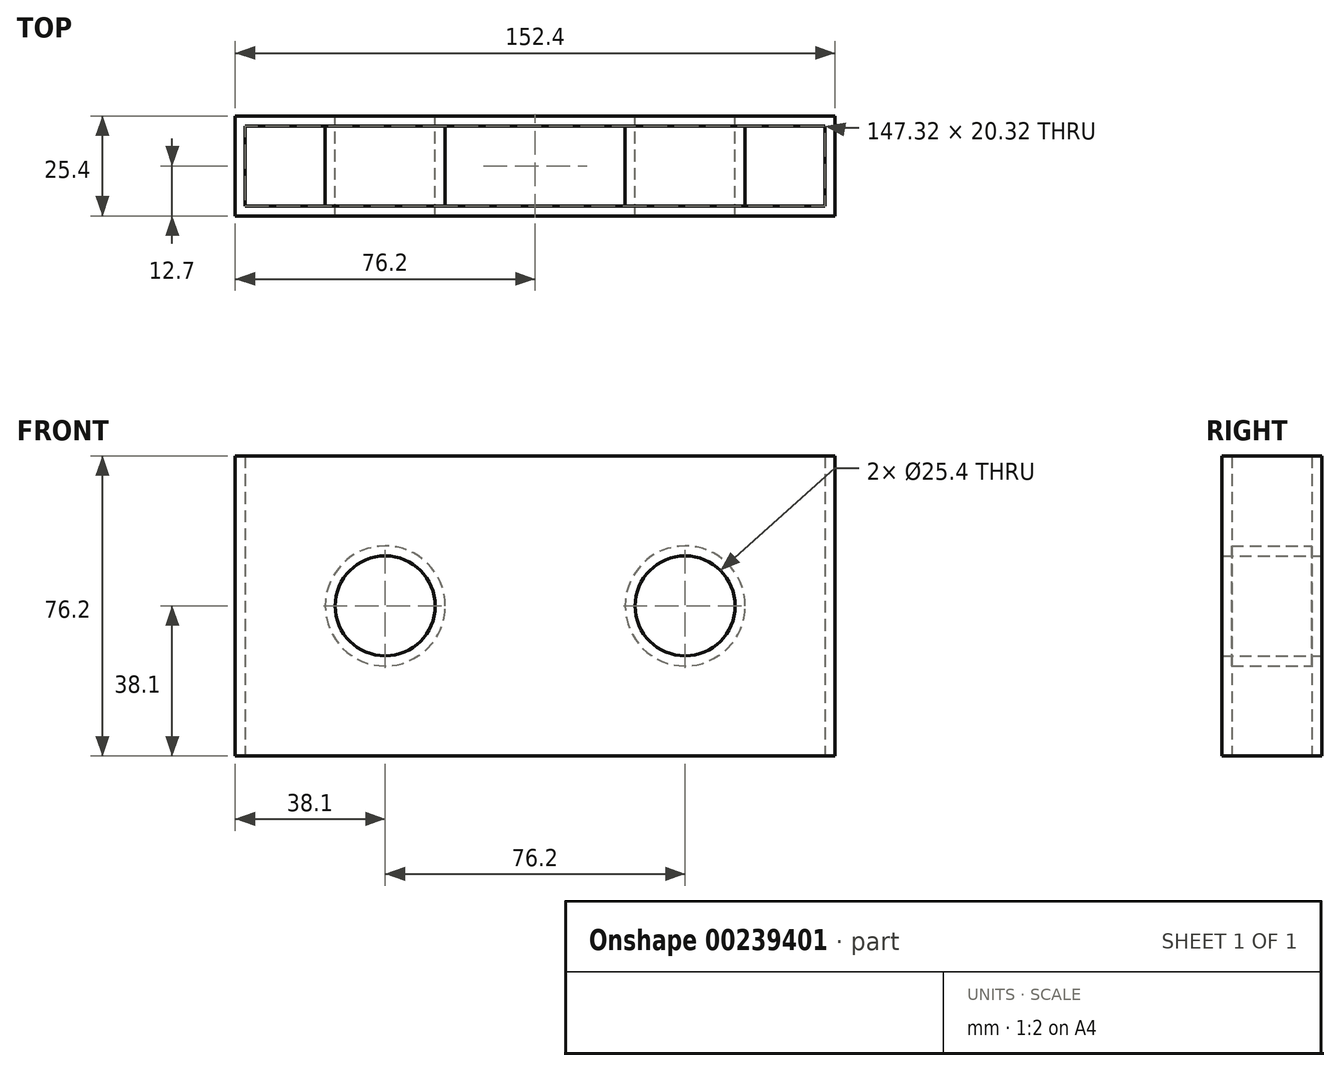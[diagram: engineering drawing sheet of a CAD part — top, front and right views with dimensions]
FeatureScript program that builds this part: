
annotation { "Feature Type Name" : "Feature", "Feature Type Description" : "" }
export const myFeature = defineFeature(function(context is Context, id is Id, definition is map)
    precondition{}
    {
        {
            var Q0;
            Q0=qCreatedBy(makeId("Front.planeOp"),FACE);
            var sketch = newSketch(context, id + "F0", { "sketchPlane" : qUnion([Q0])});
            skLineSegment(sketch, "E0.bottom", {"start": v(-76.2, 38.1) * mm, "end": v(76.2, 38.1) * mm});
            skLineSegment(sketch, "E0.top", {"start": v(-76.2, -38.1) * mm, "end": v(76.2, -38.1) * mm});
            skLineSegment(sketch, "E0.left", {"start": v(-76.2, 38.1) * mm, "end": v(-76.2, -38.1) * mm});
            skLineSegment(sketch, "E0.right", {"start": v(76.2, 38.1) * mm, "end": v(76.2, -38.1) * mm});
            skPoint(sketch, "E0.middle", {"position": v(0, 0) * mm});
            skCircle(sketch, "E1", {"center": v(38.1, 0) * mm, "radius": 12.7 * mm});
            skCircle(sketch, "E2", {"center": v(-38.1, 0) * mm, "radius": 12.7 * mm});
            skSolve(sketch);
        }
        {
            var Q0;
            Q0=makeQuery(id+"F0.imprint","IMPRINT",FACE,{"disambiguationData":[TD([[makeQuery(id+"F0.imprint","IMPRINT",EDGE,{"derivedFrom":sQuery(id+"F0.wireOp",EDGE,"E0.bottom")}),-1.0]])]});
            extrude(context, id + "F1", {"entities" : qUnion([Q0]), "depth" : 25.4 * mm});
        }
        {
            var Q0;
            Q0=makeQuery(id+"F1.opExtrude","SWEPT_FACE",FACE,{"disambiguationData":[OSD([sQuery(id+"F0.wireOp",EDGE,"E0.bottom")])]});
            var Q1;
            Q1=makeQuery(id+"F1.opExtrude","SWEPT_FACE",FACE,{"disambiguationData":[OSD([sQuery(id+"F0.wireOp",EDGE,"E0.top")])]});
            shell(context, id + "F2", {"entities" : qUnion([Q0, Q1]), "thickness" : 2.54 * mm});
        }
    });
